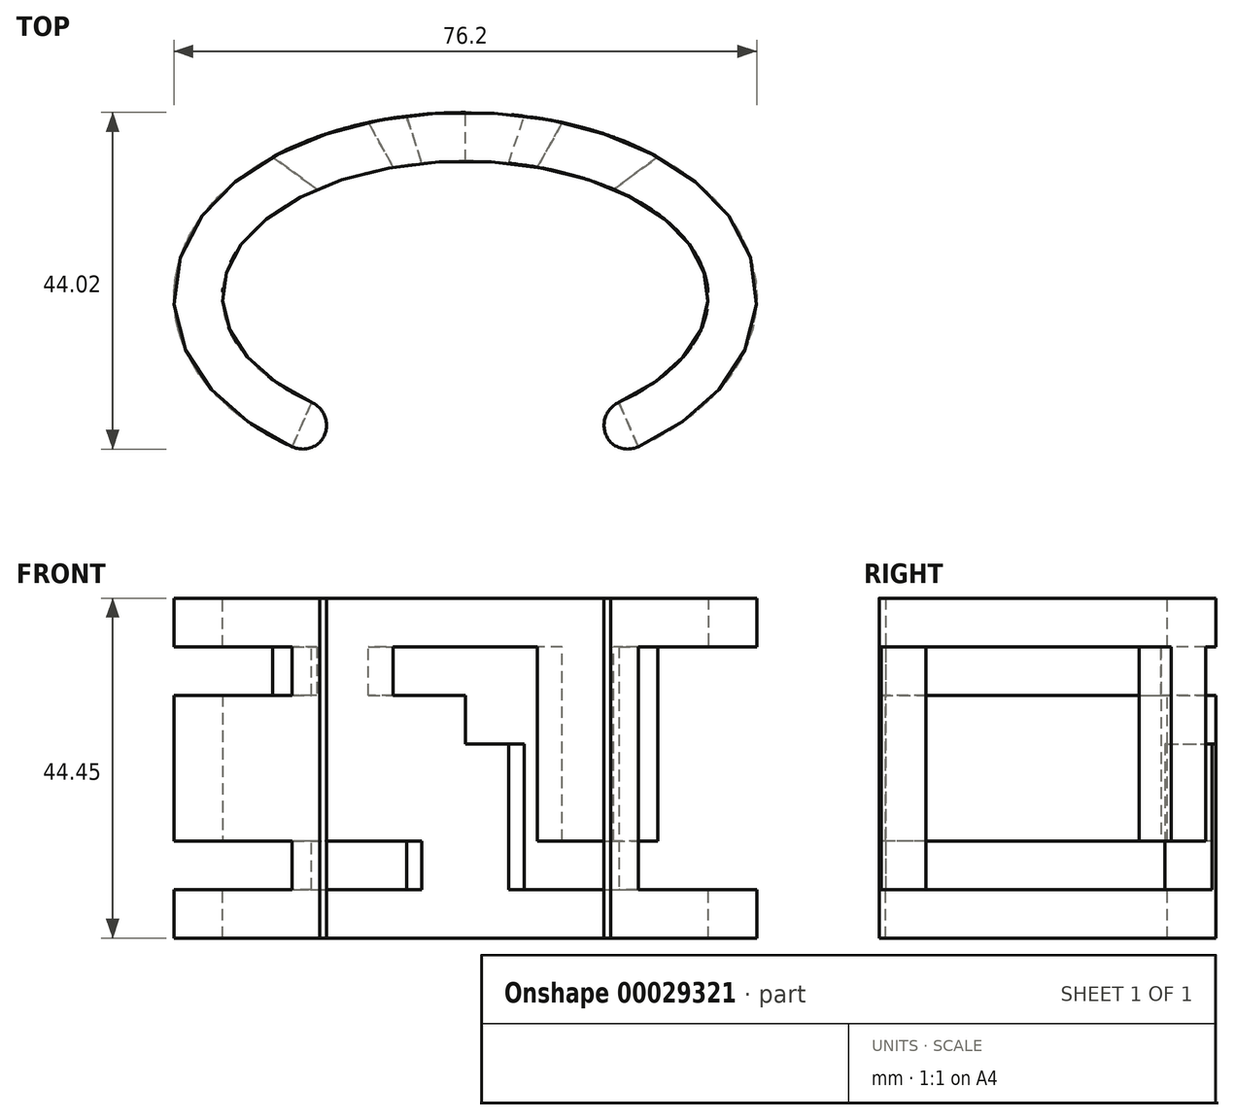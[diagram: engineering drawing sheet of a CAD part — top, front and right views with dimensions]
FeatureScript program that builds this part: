
annotation { "Feature Type Name" : "Feature", "Feature Type Description" : "" }
export const myFeature = defineFeature(function(context is Context, id is Id, definition is map)
    precondition{}
    {
        {
            var Q0;
            Q0=qCreatedBy(makeId("Top.planeOp"),FACE);
            var sketch = newSketch(context, id + "F0", { "sketchPlane" : qUnion([Q0])});
            skEllipse(sketch, "E0", {"center": v(0, 0) * mm, "majorRadius": 31.75 * mm, "minorRadius": 17.78 * mm, "majorAxis": v(-1, 0)});
            skSolve(sketch);
        }
        {
            var Q0;
            Q0=qCreatedBy(makeId("Front.planeOp"),FACE);
            var sketch = newSketch(context, id + "F1", { "sketchPlane" : qUnion([Q0])});
            skLineSegment(sketch, "E1.bottom", {"start": v(-31.75, 0) * mm, "end": v(-38.1, 0) * mm});
            skLineSegment(sketch, "E1.top", {"start": v(-31.75, 38.1) * mm, "end": v(-38.1, 38.1) * mm});
            skLineSegment(sketch, "E1.left", {"start": v(-31.75, 0) * mm, "end": v(-31.75, 38.1) * mm});
            skLineSegment(sketch, "E1.right", {"start": v(-38.1, 0) * mm, "end": v(-38.1, 38.1) * mm});
            skSolve(sketch);
        }
        {
            var Q0;
            Q0=makeQuery(id+"F1.imprint","IMPRINT",FACE,{"disambiguationData":[TD([[makeQuery(id+"F1.imprint","IMPRINT",EDGE,{"derivedFrom":sQuery(id+"F1.wireOp",EDGE,"E1.bottom")}),-1.0]])]});
            var Q1;
            Q1=sQuery(id+"F0.wireOp",EDGE,"E0");
            sweep(context, id + "F2", {"profiles" : qUnion([Q0]), "path" : qUnion([Q1])});
        }
        {
            var Q0;
            Q0=qCreatedBy(makeId("Front.planeOp"),FACE);
            var sketch = newSketch(context, id + "F3", { "sketchPlane" : qUnion([Q0])});
            skLineSegment(sketch, "E2", {"start": v(0, 0) * mm, "end": v(0, 6.35) * mm});
            skLineSegment(sketch, "E3.bottom", {"start": v(0, 6.35) * mm, "end": v(-38.1, 6.35) * mm});
            skLineSegment(sketch, "E3.top", {"start": v(0, 38.1) * mm, "end": v(-38.1, 38.1) * mm});
            skLineSegment(sketch, "E3.left", {"start": v(0, 6.35) * mm, "end": v(0, 38.1) * mm});
            skLineSegment(sketch, "E3.right", {"start": v(-38.1, 6.35) * mm, "end": v(-38.1, 38.1) * mm});
            skLineSegment(sketch, "E4.MirrorCS", {"start": v(38.1, 6.35) * mm, "end": v(38.1, 38.1) * mm});
            skLineSegment(sketch, "E5.MirrorCS", {"start": v(0, 38.1) * mm, "end": v(38.1, 38.1) * mm});
            skLineSegment(sketch, "E6.MirrorCS", {"start": v(0, 6.35) * mm, "end": v(38.1, 6.35) * mm});
            skLineSegment(sketch, "E7.top", {"start": v(0, 12.7) * mm, "end": v(38.1, 12.7) * mm});
            skLineSegment(sketch, "E7.left", {"start": v(0, 6.35) * mm, "end": v(0, 12.7) * mm});
            skLineSegment(sketch, "E7.right", {"start": v(38.1, 6.35) * mm, "end": v(38.1, 12.7) * mm});
            skLineSegment(sketch, "E8.top", {"start": v(0, 19.05) * mm, "end": v(38.1, 19.05) * mm});
            skLineSegment(sketch, "E8.left", {"start": v(0, 12.7) * mm, "end": v(0, 19.05) * mm});
            skLineSegment(sketch, "E8.right", {"start": v(38.1, 12.7) * mm, "end": v(38.1, 19.05) * mm});
            skLineSegment(sketch, "E9.top", {"start": v(0, 25.4) * mm, "end": v(38.1, 25.4) * mm});
            skLineSegment(sketch, "E9.left", {"start": v(0, 19.05) * mm, "end": v(0, 25.4) * mm});
            skLineSegment(sketch, "E9.right", {"start": v(38.1, 19.05) * mm, "end": v(38.1, 25.4) * mm});
            skLineSegment(sketch, "E10.top", {"start": v(0, 31.75) * mm, "end": v(38.1, 31.75) * mm});
            skLineSegment(sketch, "E10.left", {"start": v(0, 25.4) * mm, "end": v(0, 31.75) * mm});
            skLineSegment(sketch, "E10.right", {"start": v(38.1, 25.4) * mm, "end": v(38.1, 31.75) * mm});
            skLineSegment(sketch, "E11.MirrorCS", {"start": v(0, 12.7) * mm, "end": v(-38.1, 12.7) * mm});
            skLineSegment(sketch, "E12.MirrorCS", {"start": v(0, 19.05) * mm, "end": v(-38.1, 19.05) * mm});
            skLineSegment(sketch, "E13.MirrorCS", {"start": v(0, 25.4) * mm, "end": v(-38.1, 25.4) * mm});
            skLineSegment(sketch, "E14.MirrorCS", {"start": v(0, 31.75) * mm, "end": v(-38.1, 31.75) * mm});
            skSolve(sketch);
        }
        {
            var Q0;
            Q0=makeQuery(id+"F2.opSweep","SWEPT_FACE",FACE,{"disambiguationData":[OSD([sQuery(id+"F0.wireOp",EDGE,"E0"),sQuery(id+"F1.wireOp",EDGE,"E1.top")])]});
            extrude(context, id + "F4", {"entities" : qUnion([Q0]), "operationType" : NewBodyOperationType.ADD, "depth" : 6.35 * mm});
        }
        {
            var Q0;
            Q0=makeQuery(id+"F3.imprint","IMPRINT",FACE,{"disambiguationData":[TD([[makeQuery(id+"F3.imprint","IMPRINT",EDGE,{"derivedFrom":sQuery(id+"F3.wireOp",EDGE,"E3.left")}),-1.0]])]});
            var Q1;
            Q1=makeQuery(id+"F3.imprint","IMPRINT",FACE,{"disambiguationData":[TD([[makeQuery(id+"F3.imprint","IMPRINT",EDGE,{"derivedFrom":sQuery(id+"F3.wireOp",EDGE,"E8.top")}),1.0]])]});
            var Q2;
            Q2=makeQuery(id+"F3.imprint","IMPRINT",FACE,{"disambiguationData":[TD([[makeQuery(id+"F3.imprint","IMPRINT",EDGE,{"derivedFrom":sQuery(id+"F3.wireOp",EDGE,"E6.MirrorCS")}),1.0]])]});
            var Q3;
            {var subQ2=sQuery(id+"F3.wireOp",EDGE,"E3.top");Q3=makeQuery(id+"F3.imprint","IMPRINT",FACE,{"disambiguationData":[TD([[makeQuery(id+"F3.imprint","IMPRINT",EDGE,{"derivedFrom":subQ2}),1.0]])]});}
            var Q4;
            Q4=makeQuery(id+"F3.imprint","IMPRINT",FACE,{"disambiguationData":[TD([[makeQuery(id+"F3.imprint","IMPRINT",EDGE,{"derivedFrom":sQuery(id+"F3.wireOp",EDGE,"E9.left")}),1.0]])]});
            var Q5;
            {var subQ2=sQuery(id+"F3.wireOp",EDGE,"E3.bottom");Q5=makeQuery(id+"F3.imprint","IMPRINT",FACE,{"disambiguationData":[TD([[makeQuery(id+"F3.imprint","IMPRINT",EDGE,{"derivedFrom":subQ2}),-1.0]])]});}
            extrude(context, id + "F5", {"entities" : qUnion([Q0, Q1, Q2, Q3, Q4, Q5]), "operationType" : NewBodyOperationType.REMOVE, "oppositeDirection" : true, "depth" : 50.8 * mm});
        }
        {
            var Q0;
            {var subQ2=sQuery(id+"F3.wireOp",EDGE,"E3.top");Q0=makeQuery(id+"F3.imprint","IMPRINT",FACE,{"disambiguationData":[TD([[makeQuery(id+"F3.imprint","IMPRINT",EDGE,{"derivedFrom":subQ2}),1.0]])]});}
            var Q1;
            Q1=makeQuery(id+"F3.imprint","IMPRINT",FACE,{"disambiguationData":[TD([[makeQuery(id+"F3.imprint","IMPRINT",EDGE,{"derivedFrom":sQuery(id+"F3.wireOp",EDGE,"E3.left")}),-1.0]])]});
            var Q2;
            Q2=makeQuery(id+"F3.imprint","IMPRINT",FACE,{"disambiguationData":[TD([[makeQuery(id+"F3.imprint","IMPRINT",EDGE,{"derivedFrom":sQuery(id+"F3.wireOp",EDGE,"E9.left")}),1.0]])]});
            var Q3;
            Q3=makeQuery(id+"F3.imprint","IMPRINT",FACE,{"disambiguationData":[TD([[makeQuery(id+"F3.imprint","IMPRINT",EDGE,{"derivedFrom":sQuery(id+"F3.wireOp",EDGE,"E8.top")}),1.0]])]});
            var Q4;
            {var subQ2=sQuery(id+"F3.wireOp",EDGE,"E3.bottom");Q4=makeQuery(id+"F3.imprint","IMPRINT",FACE,{"disambiguationData":[TD([[makeQuery(id+"F3.imprint","IMPRINT",EDGE,{"derivedFrom":subQ2}),-1.0]])]});}
            var Q5;
            Q5=makeQuery(id+"F3.imprint","IMPRINT",FACE,{"disambiguationData":[TD([[makeQuery(id+"F3.imprint","IMPRINT",EDGE,{"derivedFrom":sQuery(id+"F3.wireOp",EDGE,"E6.MirrorCS")}),1.0]])]});
            extrude(context, id + "F6", {"entities" : qUnion([Q0, Q1, Q2, Q3, Q4, Q5]), "operationType" : NewBodyOperationType.REMOVE, "depth" : 50.8 * mm});
        }
        {
            var Q0;
            Q0=makeQuery(id+"F4.opExtrude","CAP_FACE",FACE,{"disambiguationData":[OSD([sQuery(id+"F0.wireOp",EDGE,"E0"),sQuery(id+"F1.wireOp",EDGE,"E1.top")])],"isStart":false});
            var sketch = newSketch(context, id + "F7", { "sketchPlane" : qUnion([Q0])});
            skCircle(sketch, "E15.cCircle", {"center": v(0, 0) * mm, "radius": 31.75 * mm, "construction": true});
            skLineSegment(sketch, "E15.0", {"start": v(-31.75, 31.75) * mm, "end": v(31.75, 31.75) * mm});
            skLineSegment(sketch, "E15.1", {"start": v(31.75, 31.75) * mm, "end": v(31.75, -31.75) * mm});
            skLineSegment(sketch, "E15.2", {"start": v(31.75, -31.75) * mm, "end": v(-31.75, -31.75) * mm});
            skLineSegment(sketch, "E15.3", {"start": v(-31.75, -31.75) * mm, "end": v(-31.75, 31.75) * mm});
            skPoint(sketch, "E15.0.midPoint", {"position": v(0, 31.75) * mm});
            skLineSegment(sketch, "E16", {"start": v(0, 0) * mm, "end": v(-31.75, -31.75) * mm});
            skLineSegment(sketch, "E17", {"start": v(0, 0) * mm, "end": v(31.75, -31.75) * mm});
            skSolve(sketch);
        }
        {
            var Q0;
            {var subQ0=sQuery(id+"F0.wireOp",EDGE,"E0");var subQ1=sQuery(id+"F1.wireOp",EDGE,"E1.top");var subQ5=sQuery(id+"F7.wireOp",EDGE,"E16");var subQ7=makeQuery(id+"F4.opExtrude","CAP_EDGE",EDGE,{"disambiguationData":[OSD([subQ0,subQ1,sQuery(id+"F1.wireOp",EDGE,"E1.left")])],"isStart":false});var subQ9=makeQuery(id+"F7.imprint","INTERSECT",VERTEX,{"derivedFrom":[subQ7,subQ5]});Q0=makeQuery(id+"F7.imprint","IMPRINT",FACE,{"disambiguationData":[TD([[makeQuery(id+"F7.imprint","IMPRINT",EDGE,{"disambiguationData":[TD([[subQ9,-1.0]])],"derivedFrom":subQ5}),1.0]])]});}
            var Q1;
            {var subQ1=sQuery(id+"F7.wireOp",EDGE,"E17");var subQ3=sQuery(id+"F7.wireOp",EDGE,"E16");var subQ5=makeQuery(id+"F7.imprint","INTERSECT",VERTEX,{"derivedFrom":[subQ3,subQ1]});Q1=makeQuery(id+"F7.imprint","IMPRINT",FACE,{"disambiguationData":[TD([[makeQuery(id+"F7.imprint","IMPRINT",EDGE,{"disambiguationData":[TD([[subQ5,-1.0]])],"derivedFrom":subQ3}),1.0]])]});}
            var Q2;
            {var subQ5=sQuery(id+"F7.wireOp",EDGE,"E15.2");Q2=makeQuery(id+"F7.imprint","IMPRINT",FACE,{"disambiguationData":[TD([[makeQuery(id+"F7.imprint","IMPRINT",EDGE,{"derivedFrom":subQ5}),-1.0]])]});}
            extrude(context, id + "F8", {"entities" : qUnion([Q0, Q1, Q2]), "operationType" : NewBodyOperationType.REMOVE, "oppositeDirection" : true, "depth" : 76.2 * mm});
        }
        {
            var Q0;
            Q0=makeQuery(id+"F4.opExtrude","CAP_FACE",FACE,{"disambiguationData":[OSD([sQuery(id+"F0.wireOp",EDGE,"E0"),sQuery(id+"F1.wireOp",EDGE,"E1.top")])],"isStart":false});
            var sketch = newSketch(context, id + "F9", { "sketchPlane" : qUnion([Q0])});
            skCircle(sketch, "E18.cCircle", {"center": v(0, 0) * mm, "radius": 65.83 * mm, "construction": true});
            skLineSegment(sketch, "E18.0", {"start": v(-21.4, 65.83) * mm, "end": v(21.4, 65.83) * mm});
            skLineSegment(sketch, "E18.1", {"start": v(21.4, 65.83) * mm, "end": v(56, 40.69) * mm});
            skLineSegment(sketch, "E18.2", {"start": v(56, 40.69) * mm, "end": v(69.22, 0) * mm});
            skLineSegment(sketch, "E18.3", {"start": v(69.22, 0) * mm, "end": v(56, -40.69) * mm});
            skLineSegment(sketch, "E18.4", {"start": v(56, -40.69) * mm, "end": v(21.4, -65.83) * mm});
            skLineSegment(sketch, "E18.5", {"start": v(21.4, -65.83) * mm, "end": v(-21.4, -65.83) * mm});
            skLineSegment(sketch, "E18.6", {"start": v(-21.4, -65.83) * mm, "end": v(-56, -40.69) * mm});
            skLineSegment(sketch, "E18.7", {"start": v(-56, -40.69) * mm, "end": v(-69.22, 0) * mm});
            skLineSegment(sketch, "E18.8", {"start": v(-69.22, 0) * mm, "end": v(-56, 40.69) * mm});
            skLineSegment(sketch, "E18.9", {"start": v(-56, 40.69) * mm, "end": v(-21.4, 65.83) * mm});
            skPoint(sketch, "E18.0.midPoint", {"position": v(0, 65.83) * mm});
            skLineSegment(sketch, "E19", {"start": v(0, 0) * mm, "end": v(-56, 40.69) * mm});
            skLineSegment(sketch, "E20", {"start": v(0, 0) * mm, "end": v(-21.4, 65.83) * mm});
            skLineSegment(sketch, "E21", {"start": v(0, 0) * mm, "end": v(21.4, 65.83) * mm});
            skLineSegment(sketch, "E22", {"start": v(0, 0) * mm, "end": v(56, 40.69) * mm});
            skPoint(sketch, "E23.end.orphan", {"position": v(-38.7, 53.26) * mm});
            skPoint(sketch, "E24.end.orphan", {"position": v(38.7, 53.26) * mm});
            skLineSegment(sketch, "E25", {"start": v(0, 0) * mm, "end": v(32.2, 57.98) * mm});
            skLineSegment(sketch, "E26.MirrorCS", {"start": v(0, 0) * mm, "end": v(-32.2, 57.98) * mm});
            skSolve(sketch);
        }
        {
            var Q0;
            {var subQ0=sQuery(id+"F0.wireOp",EDGE,"E0");var subQ1=sQuery(id+"F1.wireOp",EDGE,"E1.top");var subQ5=sQuery(id+"F9.wireOp",EDGE,"E19");var subQ7=makeQuery(id+"F4.opExtrude","CAP_EDGE",EDGE,{"disambiguationData":[OSD([subQ0,subQ1,sQuery(id+"F1.wireOp",EDGE,"E1.left")])],"isStart":false});var subQ9=makeQuery(id+"F9.imprint","INTERSECT",VERTEX,{"derivedFrom":[subQ7,subQ5]});Q0=makeQuery(id+"F9.imprint","IMPRINT",FACE,{"disambiguationData":[TD([[makeQuery(id+"F9.imprint","IMPRINT",EDGE,{"disambiguationData":[TD([[subQ9,-1.0]])],"derivedFrom":subQ5}),-1.0]])]});}
            var Q1;
            {var subQ0=sQuery(id+"F0.wireOp",EDGE,"E0");var subQ1=sQuery(id+"F1.wireOp",EDGE,"E1.top");var subQ5=sQuery(id+"F9.wireOp",EDGE,"E22");var subQ7=makeQuery(id+"F4.opExtrude","CAP_EDGE",EDGE,{"disambiguationData":[OSD([subQ0,subQ1,sQuery(id+"F1.wireOp",EDGE,"E1.left")])],"isStart":false});var subQ9=makeQuery(id+"F9.imprint","INTERSECT",VERTEX,{"derivedFrom":[subQ7,subQ5]});Q1=makeQuery(id+"F9.imprint","IMPRINT",FACE,{"disambiguationData":[TD([[makeQuery(id+"F9.imprint","IMPRINT",EDGE,{"disambiguationData":[TD([[subQ9,-1.0]])],"derivedFrom":subQ5}),1.0]])]});}
            extrude(context, id + "F10", {"entities" : qUnion([Q0, Q1]), "operationType" : NewBodyOperationType.ADD, "oppositeDirection" : true, "depth" : 31.75 * mm});
        }
        {
            var Q0;
            Q0=makeQuery(id+"F2.opSweep","SWEPT_FACE",FACE,{"disambiguationData":[OSD([sQuery(id+"F0.wireOp",EDGE,"E0"),sQuery(id+"F1.wireOp",EDGE,"E1.bottom")])]});
            var sketch = newSketch(context, id + "F11", { "sketchPlane" : qUnion([Q0])});
            skCircle(sketch, "E27.cCircle", {"center": v(0, 0) * mm, "radius": 65.83 * mm, "construction": true});
            skLineSegment(sketch, "E27.0", {"start": v(-21.4, 65.83) * mm, "end": v(21.4, 65.83) * mm});
            skLineSegment(sketch, "E27.1", {"start": v(21.4, 65.83) * mm, "end": v(56, 40.69) * mm});
            skLineSegment(sketch, "E27.2", {"start": v(56, 40.69) * mm, "end": v(69.22, 0) * mm});
            skLineSegment(sketch, "E27.3", {"start": v(69.22, 0) * mm, "end": v(56, -40.69) * mm});
            skLineSegment(sketch, "E27.4", {"start": v(56, -40.69) * mm, "end": v(21.4, -65.83) * mm});
            skLineSegment(sketch, "E27.5", {"start": v(21.4, -65.83) * mm, "end": v(-21.4, -65.83) * mm});
            skLineSegment(sketch, "E27.6", {"start": v(-21.4, -65.83) * mm, "end": v(-56, -40.69) * mm});
            skLineSegment(sketch, "E27.7", {"start": v(-56, -40.69) * mm, "end": v(-69.22, 0) * mm});
            skLineSegment(sketch, "E27.8", {"start": v(-69.22, 0) * mm, "end": v(-56, 40.69) * mm});
            skLineSegment(sketch, "E27.9", {"start": v(-56, 40.69) * mm, "end": v(-21.4, 65.83) * mm});
            skPoint(sketch, "E27.0.midPoint", {"position": v(0, 65.83) * mm});
            skLineSegment(sketch, "E28", {"start": v(0, 0) * mm, "end": v(-56, 40.69) * mm});
            skLineSegment(sketch, "E29", {"start": v(0, 0) * mm, "end": v(-21.4, 65.83) * mm});
            skLineSegment(sketch, "E30", {"start": v(0, 0) * mm, "end": v(21.4, 65.83) * mm});
            skLineSegment(sketch, "E31", {"start": v(0, 0) * mm, "end": v(56, 40.69) * mm});
            skPoint(sketch, "E32.end.orphan", {"position": v(-38.7, 53.26) * mm});
            skPoint(sketch, "E33.end.orphan", {"position": v(38.7, 53.26) * mm});
            skLineSegment(sketch, "E34", {"start": v(0, 0) * mm, "end": v(-20.13, 0) * mm});
            skLineSegment(sketch, "E35.MirrorCS", {"start": v(0, 0) * mm, "end": v(-21.4, -65.83) * mm});
            skLineSegment(sketch, "E36.MirrorCS", {"start": v(0, 0) * mm, "end": v(21.4, -65.83) * mm});
            skSolve(sketch);
        }
        {
            var Q0;
            {var subQ0=sQuery(id+"F0.wireOp",EDGE,"E0");var subQ1=sQuery(id+"F1.wireOp",EDGE,"E1.bottom");var subQ2=makeQuery(id+"F2.opSweep","SWEPT_EDGE",EDGE,{"disambiguationData":[OSD([subQ0,subQ1,sQuery(id+"F1.wireOp",EDGE,"E1.left")])]});var subQ5=sQuery(id+"F11.wireOp",EDGE,"E35.MirrorCS");var subQ6=makeQuery(id+"F11.imprint","INTERSECT",VERTEX,{"derivedFrom":[subQ2,subQ5]});Q0=makeQuery(id+"F11.imprint","IMPRINT",FACE,{"disambiguationData":[TD([[makeQuery(id+"F11.imprint","IMPRINT",EDGE,{"disambiguationData":[TD([[subQ6,-1.0]])],"derivedFrom":subQ5}),1.0]])]});}
            extrude(context, id + "F12", {"entities" : qUnion([Q0]), "operationType" : NewBodyOperationType.ADD, "oppositeDirection" : true, "depth" : 25.4 * mm});
        }
        {
            var Q0;
            Q0=makeQuery(id+"F8.boolean.opBoolean","INTERSECT",EDGE,{"derivedFrom":[makeQuery(id+"F4.opExtrude","SWEPT_FACE",FACE,{"disambiguationData":[OSD([sQuery(id+"F0.wireOp",EDGE,"E0"),sQuery(id+"F1.wireOp",EDGE,"E1.top"),sQuery(id+"F1.wireOp",EDGE,"E1.left")])]}),makeQuery(id+"F8.opExtrude","SWEPT_FACE",FACE,{"disambiguationData":[OSD([sQuery(id+"F7.wireOp",EDGE,"E16")])]})]});
            var Q1;
            {var subQ2=sQuery(id+"F3.wireOp",EDGE,"E9.top");var subQ3=sQuery(id+"F3.wireOp",EDGE,"E13.MirrorCS");Q1=makeQuery(id+"F8.boolean.opBoolean","INTERSECT",EDGE,{"derivedFrom":[makeQuery(id+"F6.boolean.opBoolean","SPLIT",FACE,{"disambiguationData":[TD([makeQuery(id+"F5.boolean.opBoolean","COPY",FACE,{"derivedFrom":makeQuery(id+"F5.opExtrude","SWEPT_FACE",FACE,{"disambiguationData":[OSD([subQ2,subQ3])]})})])],"derivedFrom":makeQuery(id+"F2.opSweep","SWEPT_FACE",FACE,{"disambiguationData":[OSD([sQuery(id+"F0.wireOp",EDGE,"E0"),sQuery(id+"F1.wireOp",EDGE,"E1.left")])]})}),makeQuery(id+"F8.opExtrude","SWEPT_FACE",FACE,{"disambiguationData":[OSD([sQuery(id+"F7.wireOp",EDGE,"E16")])]})]});}
            var Q2;
            {var subQ0=sQuery(id+"F3.wireOp",EDGE,"E7.top");var subQ1=sQuery(id+"F3.wireOp",EDGE,"E11.MirrorCS");Q2=makeQuery(id+"F8.boolean.opBoolean","INTERSECT",EDGE,{"derivedFrom":[makeQuery(id+"F6.boolean.opBoolean","SPLIT",FACE,{"disambiguationData":[TD([makeQuery(id+"F5.boolean.opBoolean","COPY",FACE,{"derivedFrom":makeQuery(id+"F5.opExtrude","SWEPT_FACE",FACE,{"disambiguationData":[OSD([subQ0,subQ1])]})})])],"derivedFrom":makeQuery(id+"F2.opSweep","SWEPT_FACE",FACE,{"disambiguationData":[OSD([sQuery(id+"F0.wireOp",EDGE,"E0"),sQuery(id+"F1.wireOp",EDGE,"E1.left")])]})}),makeQuery(id+"F8.opExtrude","SWEPT_FACE",FACE,{"disambiguationData":[OSD([sQuery(id+"F7.wireOp",EDGE,"E16")])]})]});}
            var Q3;
            {var subQ0=sQuery(id+"F0.wireOp",EDGE,"E0");Q3=makeQuery(id+"F8.boolean.opBoolean","INTERSECT",EDGE,{"derivedFrom":[makeQuery(id+"F6.boolean.opBoolean","SPLIT",FACE,{"disambiguationData":[TD([makeQuery(id+"F2.opSweep","SWEPT_FACE",FACE,{"disambiguationData":[OSD([subQ0,sQuery(id+"F1.wireOp",EDGE,"E1.bottom")])]})])],"derivedFrom":makeQuery(id+"F2.opSweep","SWEPT_FACE",FACE,{"disambiguationData":[OSD([subQ0,sQuery(id+"F1.wireOp",EDGE,"E1.left")])]})}),makeQuery(id+"F8.opExtrude","SWEPT_FACE",FACE,{"disambiguationData":[OSD([sQuery(id+"F7.wireOp",EDGE,"E16")])]})]});}
            var Q4;
            Q4=makeQuery(id+"F8.boolean.opBoolean","INTERSECT",EDGE,{"derivedFrom":[makeQuery(id+"F4.opExtrude","SWEPT_FACE",FACE,{"disambiguationData":[OSD([sQuery(id+"F0.wireOp",EDGE,"E0"),sQuery(id+"F1.wireOp",EDGE,"E1.top"),sQuery(id+"F1.wireOp",EDGE,"E1.left")])]}),makeQuery(id+"F8.opExtrude","SWEPT_FACE",FACE,{"disambiguationData":[OSD([sQuery(id+"F7.wireOp",EDGE,"E17")])]})]});
            var Q5;
            {var subQ2=sQuery(id+"F3.wireOp",EDGE,"E9.top");var subQ3=sQuery(id+"F3.wireOp",EDGE,"E13.MirrorCS");Q5=makeQuery(id+"F8.boolean.opBoolean","INTERSECT",EDGE,{"derivedFrom":[makeQuery(id+"F6.boolean.opBoolean","SPLIT",FACE,{"disambiguationData":[TD([makeQuery(id+"F5.boolean.opBoolean","COPY",FACE,{"derivedFrom":makeQuery(id+"F5.opExtrude","SWEPT_FACE",FACE,{"disambiguationData":[OSD([subQ2,subQ3])]})})])],"derivedFrom":makeQuery(id+"F2.opSweep","SWEPT_FACE",FACE,{"disambiguationData":[OSD([sQuery(id+"F0.wireOp",EDGE,"E0"),sQuery(id+"F1.wireOp",EDGE,"E1.left")])]})}),makeQuery(id+"F8.opExtrude","SWEPT_FACE",FACE,{"disambiguationData":[OSD([sQuery(id+"F7.wireOp",EDGE,"E17")])]})]});}
            var Q6;
            {var subQ0=sQuery(id+"F3.wireOp",EDGE,"E7.top");var subQ1=sQuery(id+"F3.wireOp",EDGE,"E11.MirrorCS");Q6=makeQuery(id+"F8.boolean.opBoolean","INTERSECT",EDGE,{"derivedFrom":[makeQuery(id+"F6.boolean.opBoolean","SPLIT",FACE,{"disambiguationData":[TD([makeQuery(id+"F5.boolean.opBoolean","COPY",FACE,{"derivedFrom":makeQuery(id+"F5.opExtrude","SWEPT_FACE",FACE,{"disambiguationData":[OSD([subQ0,subQ1])]})})])],"derivedFrom":makeQuery(id+"F2.opSweep","SWEPT_FACE",FACE,{"disambiguationData":[OSD([sQuery(id+"F0.wireOp",EDGE,"E0"),sQuery(id+"F1.wireOp",EDGE,"E1.left")])]})}),makeQuery(id+"F8.opExtrude","SWEPT_FACE",FACE,{"disambiguationData":[OSD([sQuery(id+"F7.wireOp",EDGE,"E17")])]})]});}
            var Q7;
            {var subQ0=sQuery(id+"F0.wireOp",EDGE,"E0");Q7=makeQuery(id+"F8.boolean.opBoolean","INTERSECT",EDGE,{"derivedFrom":[makeQuery(id+"F6.boolean.opBoolean","SPLIT",FACE,{"disambiguationData":[TD([makeQuery(id+"F2.opSweep","SWEPT_FACE",FACE,{"disambiguationData":[OSD([subQ0,sQuery(id+"F1.wireOp",EDGE,"E1.bottom")])]})])],"derivedFrom":makeQuery(id+"F2.opSweep","SWEPT_FACE",FACE,{"disambiguationData":[OSD([subQ0,sQuery(id+"F1.wireOp",EDGE,"E1.left")])]})}),makeQuery(id+"F8.opExtrude","SWEPT_FACE",FACE,{"disambiguationData":[OSD([sQuery(id+"F7.wireOp",EDGE,"E17")])]})]});}
            var Q8;
            {var subQ0=sQuery(id+"F0.wireOp",EDGE,"E0");Q8=makeQuery(id+"F8.boolean.opBoolean","INTERSECT",EDGE,{"derivedFrom":[makeQuery(id+"F6.boolean.opBoolean","SPLIT",FACE,{"disambiguationData":[TD([makeQuery(id+"F2.opSweep","SWEPT_FACE",FACE,{"disambiguationData":[OSD([subQ0,sQuery(id+"F1.wireOp",EDGE,"E1.bottom")])]})])],"derivedFrom":makeQuery(id+"F2.opSweep","SWEPT_FACE",FACE,{"disambiguationData":[OSD([subQ0,sQuery(id+"F1.wireOp",EDGE,"E1.right")])]})}),makeQuery(id+"F8.opExtrude","SWEPT_FACE",FACE,{"disambiguationData":[OSD([sQuery(id+"F7.wireOp",EDGE,"E17")])]})]});}
            var Q9;
            {var subQ0=sQuery(id+"F3.wireOp",EDGE,"E7.top");var subQ1=sQuery(id+"F3.wireOp",EDGE,"E11.MirrorCS");Q9=makeQuery(id+"F8.boolean.opBoolean","INTERSECT",EDGE,{"derivedFrom":[makeQuery(id+"F6.boolean.opBoolean","SPLIT",FACE,{"disambiguationData":[TD([makeQuery(id+"F5.boolean.opBoolean","COPY",FACE,{"derivedFrom":makeQuery(id+"F5.opExtrude","SWEPT_FACE",FACE,{"disambiguationData":[OSD([subQ0,subQ1])]})})])],"derivedFrom":makeQuery(id+"F2.opSweep","SWEPT_FACE",FACE,{"disambiguationData":[OSD([sQuery(id+"F0.wireOp",EDGE,"E0"),sQuery(id+"F1.wireOp",EDGE,"E1.right")])]})}),makeQuery(id+"F8.opExtrude","SWEPT_FACE",FACE,{"disambiguationData":[OSD([sQuery(id+"F7.wireOp",EDGE,"E17")])]})]});}
            var Q10;
            {var subQ2=sQuery(id+"F3.wireOp",EDGE,"E9.top");var subQ3=sQuery(id+"F3.wireOp",EDGE,"E13.MirrorCS");Q10=makeQuery(id+"F8.boolean.opBoolean","INTERSECT",EDGE,{"derivedFrom":[makeQuery(id+"F6.boolean.opBoolean","SPLIT",FACE,{"disambiguationData":[TD([makeQuery(id+"F5.boolean.opBoolean","COPY",FACE,{"derivedFrom":makeQuery(id+"F5.opExtrude","SWEPT_FACE",FACE,{"disambiguationData":[OSD([subQ2,subQ3])]})})])],"derivedFrom":makeQuery(id+"F2.opSweep","SWEPT_FACE",FACE,{"disambiguationData":[OSD([sQuery(id+"F0.wireOp",EDGE,"E0"),sQuery(id+"F1.wireOp",EDGE,"E1.right")])]})}),makeQuery(id+"F8.opExtrude","SWEPT_FACE",FACE,{"disambiguationData":[OSD([sQuery(id+"F7.wireOp",EDGE,"E17")])]})]});}
            var Q11;
            Q11=makeQuery(id+"F8.boolean.opBoolean","INTERSECT",EDGE,{"derivedFrom":[makeQuery(id+"F4.opExtrude","SWEPT_FACE",FACE,{"disambiguationData":[OSD([sQuery(id+"F0.wireOp",EDGE,"E0"),sQuery(id+"F1.wireOp",EDGE,"E1.top"),sQuery(id+"F1.wireOp",EDGE,"E1.right")])]}),makeQuery(id+"F8.opExtrude","SWEPT_FACE",FACE,{"disambiguationData":[OSD([sQuery(id+"F7.wireOp",EDGE,"E17")])]})]});
            var Q12;
            Q12=makeQuery(id+"F8.boolean.opBoolean","INTERSECT",EDGE,{"derivedFrom":[makeQuery(id+"F4.opExtrude","SWEPT_FACE",FACE,{"disambiguationData":[OSD([sQuery(id+"F0.wireOp",EDGE,"E0"),sQuery(id+"F1.wireOp",EDGE,"E1.top"),sQuery(id+"F1.wireOp",EDGE,"E1.right")])]}),makeQuery(id+"F8.opExtrude","SWEPT_FACE",FACE,{"disambiguationData":[OSD([sQuery(id+"F7.wireOp",EDGE,"E16")])]})]});
            var Q13;
            {var subQ2=sQuery(id+"F3.wireOp",EDGE,"E9.top");var subQ3=sQuery(id+"F3.wireOp",EDGE,"E13.MirrorCS");Q13=makeQuery(id+"F8.boolean.opBoolean","INTERSECT",EDGE,{"derivedFrom":[makeQuery(id+"F6.boolean.opBoolean","SPLIT",FACE,{"disambiguationData":[TD([makeQuery(id+"F5.boolean.opBoolean","COPY",FACE,{"derivedFrom":makeQuery(id+"F5.opExtrude","SWEPT_FACE",FACE,{"disambiguationData":[OSD([subQ2,subQ3])]})})])],"derivedFrom":makeQuery(id+"F2.opSweep","SWEPT_FACE",FACE,{"disambiguationData":[OSD([sQuery(id+"F0.wireOp",EDGE,"E0"),sQuery(id+"F1.wireOp",EDGE,"E1.right")])]})}),makeQuery(id+"F8.opExtrude","SWEPT_FACE",FACE,{"disambiguationData":[OSD([sQuery(id+"F7.wireOp",EDGE,"E16")])]})]});}
            var Q14;
            {var subQ0=sQuery(id+"F3.wireOp",EDGE,"E7.top");var subQ1=sQuery(id+"F3.wireOp",EDGE,"E11.MirrorCS");Q14=makeQuery(id+"F8.boolean.opBoolean","INTERSECT",EDGE,{"derivedFrom":[makeQuery(id+"F6.boolean.opBoolean","SPLIT",FACE,{"disambiguationData":[TD([makeQuery(id+"F5.boolean.opBoolean","COPY",FACE,{"derivedFrom":makeQuery(id+"F5.opExtrude","SWEPT_FACE",FACE,{"disambiguationData":[OSD([subQ0,subQ1])]})})])],"derivedFrom":makeQuery(id+"F2.opSweep","SWEPT_FACE",FACE,{"disambiguationData":[OSD([sQuery(id+"F0.wireOp",EDGE,"E0"),sQuery(id+"F1.wireOp",EDGE,"E1.right")])]})}),makeQuery(id+"F8.opExtrude","SWEPT_FACE",FACE,{"disambiguationData":[OSD([sQuery(id+"F7.wireOp",EDGE,"E16")])]})]});}
            var Q15;
            {var subQ0=sQuery(id+"F0.wireOp",EDGE,"E0");Q15=makeQuery(id+"F8.boolean.opBoolean","INTERSECT",EDGE,{"derivedFrom":[makeQuery(id+"F6.boolean.opBoolean","SPLIT",FACE,{"disambiguationData":[TD([makeQuery(id+"F2.opSweep","SWEPT_FACE",FACE,{"disambiguationData":[OSD([subQ0,sQuery(id+"F1.wireOp",EDGE,"E1.bottom")])]})])],"derivedFrom":makeQuery(id+"F2.opSweep","SWEPT_FACE",FACE,{"disambiguationData":[OSD([subQ0,sQuery(id+"F1.wireOp",EDGE,"E1.right")])]})}),makeQuery(id+"F8.opExtrude","SWEPT_FACE",FACE,{"disambiguationData":[OSD([sQuery(id+"F7.wireOp",EDGE,"E16")])]})]});}
            fillet(context, id + "F13", {"entities" : qUnion([Q0, Q1, Q2, Q3, Q4, Q5, Q6, Q7, Q8, Q9, Q10, Q11, Q12, Q13, Q14, Q15]), "radius" : 3.3 * mm, "tangentPropagation" : true, "allowEdgeOverflow" : false});
        }
        {
            var Q0;
            Q0=makeQuery(id+"F4.opExtrude","CAP_FACE",FACE,{"disambiguationData":[OSD([sQuery(id+"F0.wireOp",EDGE,"E0"),sQuery(id+"F1.wireOp",EDGE,"E1.top")])],"isStart":false});
            var sketch = newSketch(context, id + "F14", { "sketchPlane" : qUnion([Q0])});
            skLineSegment(sketch, "E37", {"start": v(0, 24.13) * mm, "end": v(0, -23.84) * mm});
            skLineSegment(sketch, "E38", {"start": v(-20.08, -13.77) * mm, "end": v(-22.62, -19.6) * mm});
            skLineSegment(sketch, "E39.MirrorCS", {"start": v(20.08, -13.77) * mm, "end": v(22.62, -19.6) * mm});
            skSolve(sketch);
        }
        {
            var Q0;
            Q0=makeQuery(id+"F14.imprint","IMPRINT",FACE,{"disambiguationData":[TD([[makeQuery(id+"F14.imprint","IMPRINT",EDGE,{"derivedFrom":sQuery(id+"F14.wireOp",EDGE,"E38")}),1.0]])]});
            var Q1;
            Q1=makeQuery(id+"F14.imprint","IMPRINT",FACE,{"disambiguationData":[TD([[makeQuery(id+"F14.imprint","IMPRINT",EDGE,{"derivedFrom":sQuery(id+"F14.wireOp",EDGE,"E39.MirrorCS")}),-1.0]])]});
            extrude(context, id + "F15", {"entities" : qUnion([Q0, Q1]), "operationType" : NewBodyOperationType.ADD, "oppositeDirection" : true, "depth" : 38.1 * mm});
        }
    });
